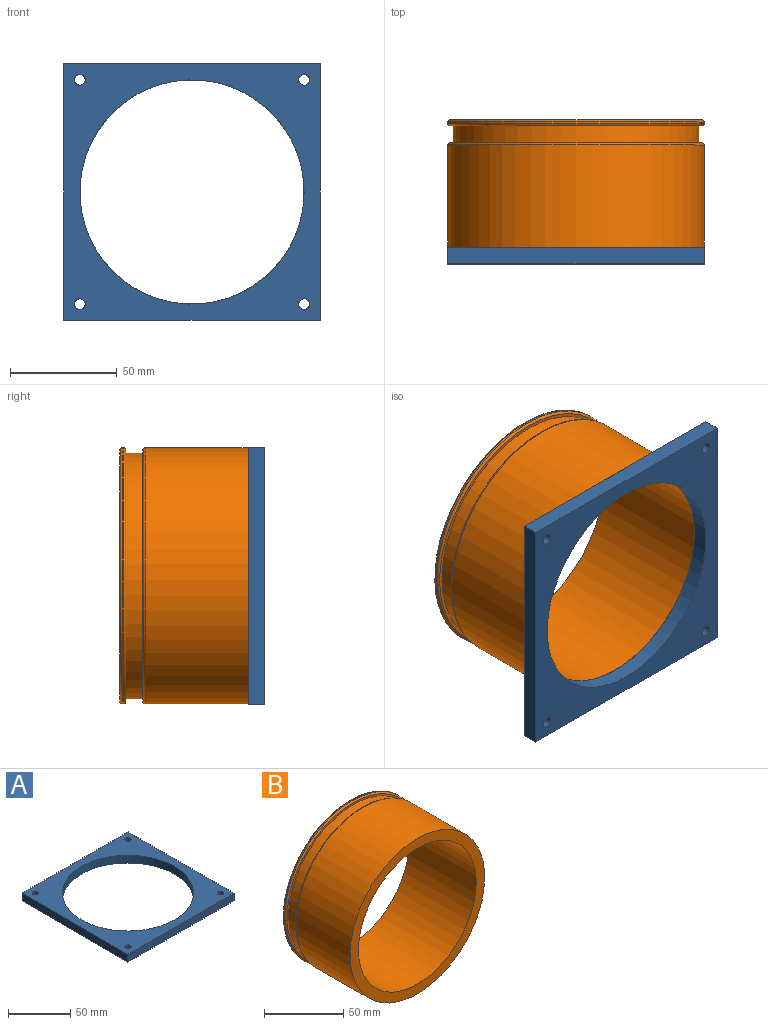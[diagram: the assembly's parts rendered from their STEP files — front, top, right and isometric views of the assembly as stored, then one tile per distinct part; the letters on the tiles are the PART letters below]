
ASSEMBLY  parts=2 mates=1
PART A: 11 faces, bbox 120x120x7.5 mm
  f0: plane 120x7.5mm, normal (0,-1,0), area 900mm2, adj f1,f4,f5,f6
  f1: plane 120x7.5mm, normal (1,0,0), area 900mm2, adj f0,f2,f5,f6
  f2: plane 120x7.5mm, normal (0,1,0), area 900mm2, adj f1,f4,f5,f6
  f3: cylinder r=52.5mm len=105mm, axis (0,0,1), area 2474mm2, adj f5,f6
  f4: plane 120x7.5mm, normal (-1,0,0), area 900mm2, adj f0,f2,f5,f6
  f5: plane 120x120mm, normal (0,0,1), area 5662.4mm2, adj f0,f1,f2,f3,f4,f7,f8,f9
  f6: plane 120x120mm, normal (0,0,-1), area 5662.4mm2, adj f0,f1,f2,f3,f4,f7,f8,f9
  f7: cylinder r=2.5mm len=7.5mm, axis (0,0,-1), area 117.8mm2, adj f5,f6
  f8: cylinder r=2.5mm len=7.5mm, axis (0,0,-1), area 117.8mm2, adj f5,f6
  f9: cylinder r=2.5mm len=7.5mm, axis (0,0,-1), area 117.8mm2, adj f5,f6
  f10: cylinder r=2.5mm len=7.5mm, axis (0,0,-1), area 117.8mm2, adj f5,f6
PART B: 11 faces, bbox 129.9x60x129.9 mm
  f0: plane 118x118mm, normal (0,1,0), area 549mm2, adj f1,f10
  f1: torus R=59mm, axis (0,1,0), area 588.6mm2, adj f0,f2
  f2: cylinder r=60mm len=120mm, axis (0,1,0), area 18178.4mm2, adj f1,f3
  f3: plane 120x120mm, normal (0,-1,0), area 2650.7mm2, adj f2,f4
  f4: cylinder r=52.5mm len=105mm, axis (0,1,0), area 19792mm2, adj f3,f5
  f5: plane 118x118mm, normal (0,1,0), area 2276.9mm2, adj f4,f6
  f6: torus R=59mm, axis (0,1,0), area 588.6mm2, adj f5,f7
  f7: cylinder r=60mm len=120mm, axis (0,1,0), area 294.2mm2, adj f6,f8
  f8: torus R=59mm, axis (0,1,0), area 588.6mm2, adj f7,f9
  f9: plane 118x118mm, normal (0,-1,0), area 549mm2, adj f8,f10
  f10: cylinder r=57.5mm len=115mm, axis (0,1,0), area 2890.3mm2, adj f0,f9
PLACE A rot(axis=(1,0,0),90deg) t=(85.01,54.01,-7.25)mm
PLACE B t=(-81.79,-79.07,-22.25)mm
MATE fastened A.f3 <-> B.f1  axis (0,1,0) through (70.01,54.01,-22.25)mm
